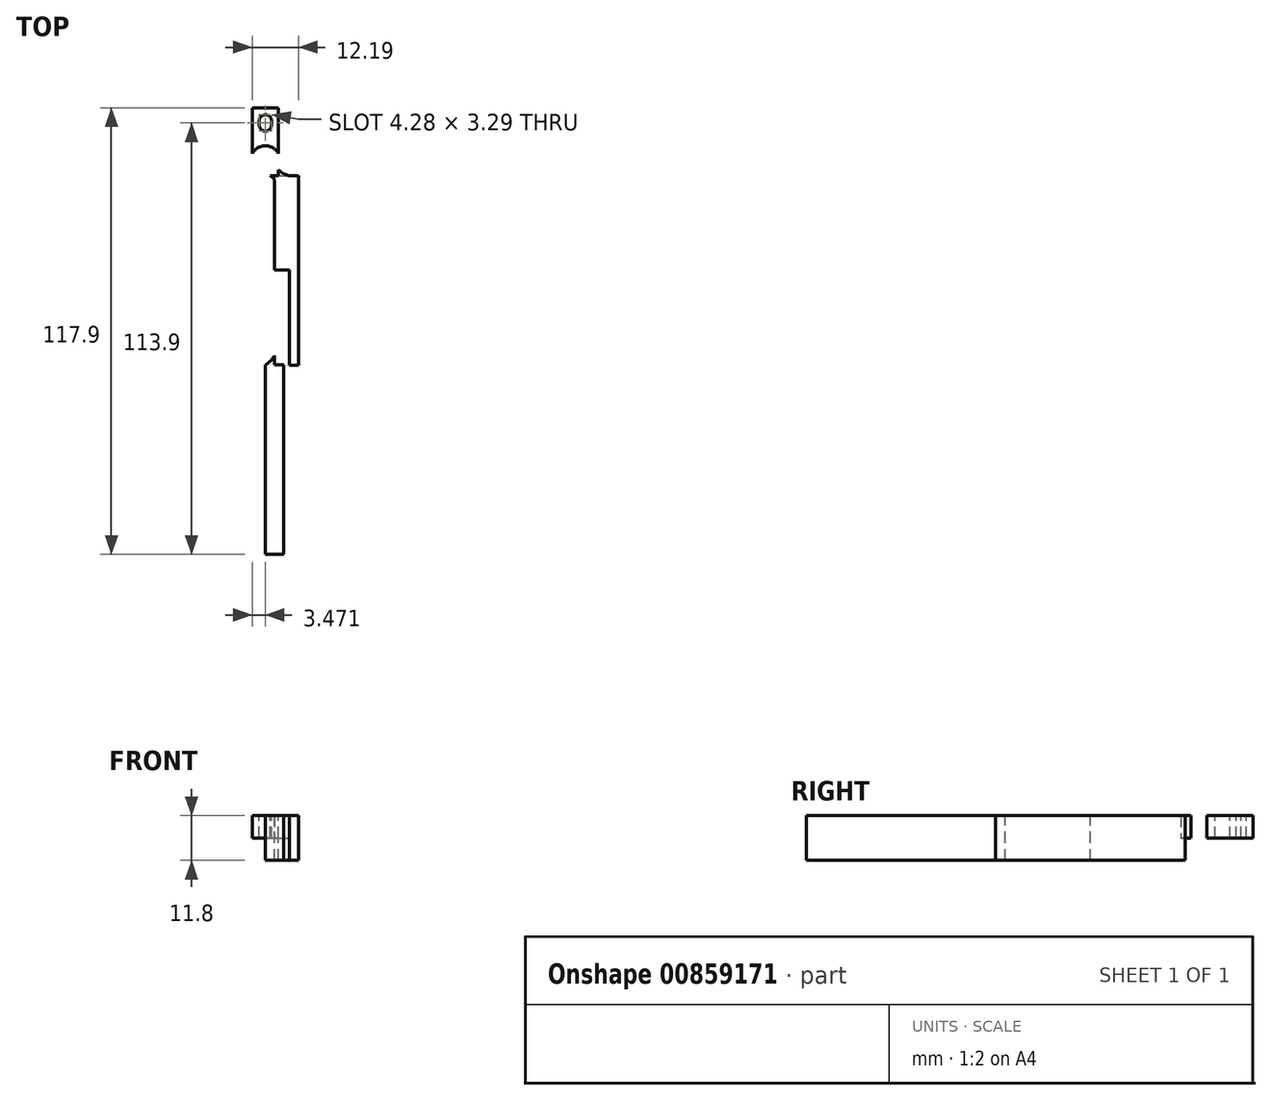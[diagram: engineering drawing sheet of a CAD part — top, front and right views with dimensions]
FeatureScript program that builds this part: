
annotation { "Feature Type Name" : "Feature", "Feature Type Description" : "" }
export const myFeature = defineFeature(function(context is Context, id is Id, definition is map)
    precondition{}
    {
        {
            var Q0;
            Q0=qCreatedBy(makeId("Top.planeOp"),FACE);
            var sketch = newSketch(context, id + "F0", { "sketchPlane" : qUnion([Q0])});
            skLineSegment(sketch, "E0.bottom", {"start": v(0, 0) * mm, "end": v(6.95, 0) * mm});
            skLineSegment(sketch, "E0.top", {"start": v(0, 17.9) * mm, "end": v(6.95, 17.9) * mm});
            skLineSegment(sketch, "E0.left", {"start": v(0, 0) * mm, "end": v(0, 17.9) * mm});
            skLineSegment(sketch, "E0.right", {"start": v(6.95, 0) * mm, "end": v(6.95, 17.9) * mm});
            skLineSegment(sketch, "E1", {"start": v(0, 0) * mm, "end": v(0, 7.85) * mm});
            skLineSegment(sketch, "E2", {"start": v(3.48, 0) * mm, "end": v(3.48, 7.85) * mm});
            skLineSegment(sketch, "E3", {"start": v(3.48, 7.85) * mm, "end": v(3.48, 6.9) * mm});
            skCircle(sketch, "E4", {"center": v(3.48, 3.92) * mm, "radius": 3.92 * mm});
            skLineSegment(sketch, "E5", {"start": v(3.47, 17.9) * mm, "end": v(3.47, 16.05) * mm});
            skLineSegment(sketch, "E6", {"start": v(3.47, 16.05) * mm, "end": v(3.48, 11.75) * mm});
            skLineSegment(sketch, "E7", {"start": v(3.47, 13.9) * mm, "end": v(3.47, 16.05) * mm});
            skLineSegment(sketch, "E8", {"start": v(3.48, 11.75) * mm, "end": v(3.47, 13.9) * mm});
            skLineSegment(sketch, "E9", {"start": v(4.55, 12.83) * mm, "end": v(4.55, 14.98) * mm});
            skLineSegment(sketch, "E10.bottom", {"start": v(3.48, 0) * mm, "end": v(1.03, 0) * mm});
            skLineSegment(sketch, "E10.top", {"start": v(3.48, -100) * mm, "end": v(1.03, -100) * mm});
            skLineSegment(sketch, "E10.left", {"start": v(3.48, 0) * mm, "end": v(3.48, -100) * mm});
            skLineSegment(sketch, "E10.right", {"start": v(1.03, 0) * mm, "end": v(1.03, -100) * mm});
            skLineSegment(sketch, "E11.bottom", {"start": v(3.48, 0) * mm, "end": v(5.93, 0) * mm});
            skLineSegment(sketch, "E11.top", {"start": v(3.48, -100) * mm, "end": v(5.93, -100) * mm});
            skLineSegment(sketch, "E11.right", {"start": v(5.93, 0) * mm, "end": v(5.93, -100) * mm});
            skLineSegment(sketch, "E12", {"start": v(5.93, 0) * mm, "end": v(5.93, 1.16) * mm});
            skLineSegment(sketch, "E13", {"start": v(1.03, 0) * mm, "end": v(1.02, 1.22) * mm});
            skLineSegment(sketch, "E14.bottom", {"start": v(6.95, 0) * mm, "end": v(9.83, -0.08) * mm});
            skLineSegment(sketch, "E14.left", {"start": v(6.95, 0) * mm, "end": v(6.95, 1.5) * mm});
            skLineSegment(sketch, "E15.right", {"start": v(5.93, -0.08) * mm, "end": v(5.93, -100) * mm});
            skLineSegment(sketch, "E16", {"start": v(3.48, 0) * mm, "end": v(3.48, -12.11) * mm});
            skLineSegment(sketch, "E17", {"start": v(3.48, 0) * mm, "end": v(3.48, -25) * mm});
            skLineSegment(sketch, "E18", {"start": v(3.48, -25) * mm, "end": v(1.03, -25) * mm});
            skLineSegment(sketch, "E19", {"start": v(1.03, -25) * mm, "end": v(1.03, -25.71) * mm});
            skLineSegment(sketch, "E20", {"start": v(1.03, -25) * mm, "end": v(1.03, -30) * mm});
            skLineSegment(sketch, "E21", {"start": v(5.93, -25) * mm, "end": v(5.93, -50) * mm});
            skPoint(sketch, "E21.startSnap0", {"position": v(2.25, -25) * mm});
            skLineSegment(sketch, "E22", {"start": v(5.93, -50) * mm, "end": v(9.83, -50.04) * mm});
            skLineSegment(sketch, "E23", {"start": v(3.48, -50) * mm, "end": v(1.03, -50) * mm});
            skLineSegment(sketch, "E24", {"start": v(5.93, -25) * mm, "end": v(9.83, -25) * mm});
            skLineSegment(sketch, "E25", {"start": v(5.93, -25) * mm, "end": v(5.93, -21.38) * mm});
            skLineSegment(sketch, "E26", {"start": v(5.93, -25) * mm, "end": v(5.93, -22.99) * mm});
            skLineSegment(sketch, "E27", {"start": v(3.48, -25) * mm, "end": v(3.48, -26.23) * mm});
            skLineSegment(sketch, "E28", {"start": v(5.93, -50) * mm, "end": v(5.93, -52.01) * mm});
            skLineSegment(sketch, "E29", {"start": v(3.48, -50) * mm, "end": v(3.48, -48.78) * mm});
            skLineSegment(sketch, "E30", {"start": v(5.93, -25) * mm, "end": v(5.93, -26.95) * mm});
            skLineSegment(sketch, "E31", {"start": v(3.48, -50) * mm, "end": v(5.93, -50) * mm});
            skLineSegment(sketch, "E32", {"start": v(3.48, 0) * mm, "end": v(3.48, -1.23) * mm});
            skLineSegment(sketch, "E33", {"start": v(6.95, 0) * mm, "end": v(6.95, 1.44) * mm});
            skFitSpline(sketch, "E34", {"points": [v(6.95, 1.5) * mm, v(9.83, -0.08) * mm], "startDerivative": vector(2.42, -2.4) * mm, "endDerivative": vector(3.34, -1.08) * mm});
            skLineSegment(sketch, "E35", {"start": v(1.03, 0) * mm, "end": v(1.03, -0.69) * mm});
            skLineSegment(sketch, "E36", {"start": v(1.03, 0) * mm, "end": v(1.03, -1) * mm});
            skLineSegment(sketch, "E37", {"start": v(5.92, 0) * mm, "end": v(5.93, -1.23) * mm});
            skFitSpline(sketch, "E38", {"points": [v(4.7, 0) * mm, v(5.93, -1.23) * mm], "startDerivative": vector(1.66, -0.95) * mm, "endDerivative": vector(0.86, -1.52) * mm});
            skLineSegment(sketch, "E39", {"start": v(5.93, -25) * mm, "end": v(5.93, -28.9) * mm});
            skLineSegment(sketch, "E40", {"start": v(3.48, -25) * mm, "end": v(5.93, -25) * mm});
            skLineSegment(sketch, "E41", {"start": v(5.93, -25) * mm, "end": v(5.93, -22.55) * mm});
            skLineSegment(sketch, "E42", {"start": v(5.93, -50) * mm, "end": v(5.93, -47.55) * mm});
            skFitSpline(sketch, "E43", {"points": [v(5.93, -47.55) * mm, v(3.48, -50) * mm], "startDerivative": vector(-2.07, -3.53) * mm, "endDerivative": vector(-2.94, -2.05) * mm});
            skLineSegment(sketch, "E44.left", {"start": v(5.93, -50) * mm, "end": v(5.93, -100) * mm});
            skLineSegment(sketch, "E45", {"start": v(9.83, -0.08) * mm, "end": v(9.83, -50.04) * mm});
            skLineSegment(sketch, "E46.bottom", {"start": v(9.83, -0.08) * mm, "end": v(12.2, -0.08) * mm});
            skLineSegment(sketch, "E46.top", {"start": v(9.83, -50.08) * mm, "end": v(12.2, -50.08) * mm});
            skLineSegment(sketch, "E46.left", {"start": v(9.83, -0.08) * mm, "end": v(9.83, -50.08) * mm});
            skLineSegment(sketch, "E46.right", {"start": v(12.2, -0.08) * mm, "end": v(12.2, -50.08) * mm});
            skLineSegment(sketch, "E47.bottom", {"start": v(5.93, -50) * mm, "end": v(8.3, -50) * mm});
            skLineSegment(sketch, "E47.top", {"start": v(5.93, -100) * mm, "end": v(8.3, -100) * mm});
            skLineSegment(sketch, "E47.right", {"start": v(8.3, -50) * mm, "end": v(8.3, -100) * mm});
            skLineSegment(sketch, "E48", {"start": v(8.3, -50) * mm, "end": v(12.2, -50.08) * mm});
            skLineSegment(sketch, "E49", {"start": v(8.3, -50) * mm, "end": v(8.3, -53.9) * mm});
            skFitSpline(sketch, "E50", {"points": [v(8.3, -53.9) * mm, v(10.24, -50.04) * mm], "startDerivative": vector(0.85, 4.55) * mm, "endDerivative": vector(3.1, 3.55) * mm});
            skCircle(sketch, "E51", {"center": v(3.48, 3.92) * mm, "radius": 3.28 * mm});
            skLineSegment(sketch, "E52", {"start": v(3.47, 13.9) * mm, "end": v(3.47, 12.9) * mm});
            skLineSegment(sketch, "E53", {"start": v(3.47, 13.9) * mm, "end": v(3.47, 14.9) * mm});
            skCircle(sketch, "E54", {"center": v(3.47, 13.4) * mm, "radius": 1.64 * mm});
            skArc(sketch, "E55", {"start": v(5.1, 14.7) * mm, "mid": v(1.83, 14.37) * mm, "end": v(5.1, 14.14) * mm});
            skLineSegment(sketch, "E56", {"start": v(3.48, 11.75) * mm, "end": v(1.27, 11.75) * mm});
            skLineSegment(sketch, "E57", {"start": v(3.48, 11.75) * mm, "end": v(5.93, 11.75) * mm});
            skLineSegment(sketch, "E58", {"start": v(3.47, 16.05) * mm, "end": v(1.21, 16.05) * mm});
            skLineSegment(sketch, "E59", {"start": v(3.47, 16.05) * mm, "end": v(5.69, 16.05) * mm});
            skLineSegment(sketch, "E60", {"start": v(5.11, 13.43) * mm, "end": v(5.1, 14.7) * mm});
            skLineSegment(sketch, "E61", {"start": v(1.84, 13.46) * mm, "end": v(1.83, 14.38) * mm});
            skSolve(sketch);
        }
        {
            var Q0;
            {var subQ0=sQuery(id+"F0.wireOp",EDGE,"E4");var subQ3=sQuery(id+"F0.wireOp",EDGE,"E0.right");var subQ10=makeQuery(id+"F0.imprint","INTERSECT",VERTEX,{"disambiguationData":[OD(0.0)],"derivedFrom":[subQ3,subQ0]});Q0=makeQuery(id+"F0.imprint","IMPRINT",FACE,{"disambiguationData":[TD([[makeQuery(id+"F0.imprint","IMPRINT",EDGE,{"disambiguationData":[TD([[subQ10,-1.0]])],"derivedFrom":subQ3}),1.0]])]});}
            var Q1;
            {var subQ0=sQuery(id+"F0.wireOp",EDGE,"E4");var subQ7=sQuery(id+"F0.wireOp",EDGE,"E1");var subQ10=makeQuery(id+"F0.imprint","INTERSECT",VERTEX,{"disambiguationData":[OD(0.0)],"derivedFrom":[subQ7,subQ0]});Q1=makeQuery(id+"F0.imprint","IMPRINT",FACE,{"disambiguationData":[TD([[makeQuery(id+"F0.imprint","IMPRINT",EDGE,{"disambiguationData":[TD([[subQ10,-1.0]])],"derivedFrom":subQ7}),-1.0]])]});}
            var Q2;
            {var subQ0=sQuery(id+"F0.wireOp",EDGE,"E1");var subQ1=sQuery(id+"F0.wireOp",EDGE,"E0.bottom");var subQ2=makeQuery(id+"F0.imprint","INTERSECT",VERTEX,{"derivedFrom":[subQ1,subQ0]});Q2=makeQuery(id+"F0.imprint","IMPRINT",FACE,{"disambiguationData":[TD([[makeQuery(id+"F0.imprint","IMPRINT",EDGE,{"disambiguationData":[TD([[subQ2,-1.0]])],"derivedFrom":subQ0}),-1.0]])]});}
            var Q3;
            {var subQ0=sQuery(id+"F0.wireOp",EDGE,"E10.bottom");Q3=makeQuery(id+"F0.imprint","IMPRINT",FACE,{"disambiguationData":[TD([[makeQuery(id+"F0.imprint","IMPRINT",EDGE,{"derivedFrom":subQ0}),-1.0]])]});}
            var Q4;
            {var subQ0=sQuery(id+"F0.wireOp",EDGE,"E4");var subQ1=sQuery(id+"F0.wireOp",EDGE,"E1");var subQ2=makeQuery(id+"F0.imprint","INTERSECT",VERTEX,{"disambiguationData":[OD(0.0)],"derivedFrom":[subQ1,subQ0]});Q4=makeQuery(id+"F0.imprint","IMPRINT",FACE,{"disambiguationData":[TD([[makeQuery(id+"F0.imprint","IMPRINT",EDGE,{"disambiguationData":[TD([[subQ2,-1.0]])],"derivedFrom":subQ1}),1.0]])]});}
            var Q5;
            {var subQ0=sQuery(id+"F0.wireOp",EDGE,"E4");var subQ1=sQuery(id+"F0.wireOp",EDGE,"E0.right");var subQ2=makeQuery(id+"F0.imprint","INTERSECT",VERTEX,{"disambiguationData":[OD(0.0)],"derivedFrom":[subQ1,subQ0]});Q5=makeQuery(id+"F0.imprint","IMPRINT",FACE,{"disambiguationData":[TD([[makeQuery(id+"F0.imprint","IMPRINT",EDGE,{"disambiguationData":[TD([[subQ2,-1.0]])],"derivedFrom":subQ1}),-1.0]])]});}
            var Q6;
            {var subQ5=sQuery(id+"F0.wireOp",EDGE,"E14.left");Q6=makeQuery(id+"F0.imprint","IMPRINT",FACE,{"disambiguationData":[TD([[makeQuery(id+"F0.imprint","IMPRINT",EDGE,{"derivedFrom":subQ5}),1.0]])]});}
            var Q7;
            {var subQ0=sQuery(id+"F0.wireOp",EDGE,"E11.bottom");var subQ5=makeQuery(id+"F0.imprint","INTERSECT",VERTEX,{"derivedFrom":[subQ0,sQuery(id+"F0.wireOp",EDGE,"E38")]});Q7=makeQuery(id+"F0.imprint","IMPRINT",FACE,{"disambiguationData":[TD([[makeQuery(id+"F0.imprint","IMPRINT",EDGE,{"disambiguationData":[TD([[subQ5,-1.0]])],"derivedFrom":subQ0}),1.0]])]});}
            var Q8;
            {var subQ3=sQuery(id+"F0.wireOp",EDGE,"E38");Q8=makeQuery(id+"F0.imprint","IMPRINT",FACE,{"disambiguationData":[TD([[makeQuery(id+"F0.imprint","IMPRINT",EDGE,{"derivedFrom":subQ3}),1.0]])]});}
            var Q9;
            Q9=makeQuery(id+"F0.imprint","IMPRINT",FACE,{"disambiguationData":[TD([[makeQuery(id+"F0.imprint","IMPRINT",EDGE,{"derivedFrom":sQuery(id+"F0.wireOp",EDGE,"E14.bottom")}),1.0]])]});
            extrude(context, id + "F1", {"entities" : qUnion([Q0, Q1, Q2, Q3, Q4, Q5, Q6, Q7, Q8, Q9]), "depth" : -5.9 * mm, "offsetDistance" : 25 * mm});
        }
        {
            var Q0;
            {var subQ1=sQuery(id+"F0.wireOp",EDGE,"E47.top");Q0=makeQuery(id+"F0.imprint","IMPRINT",FACE,{"disambiguationData":[TD([[makeQuery(id+"F0.imprint","IMPRINT",EDGE,{"derivedFrom":subQ1}),1.0]])]});}
            var Q1;
            Q1=makeQuery(id+"F0.imprint","IMPRINT",FACE,{"disambiguationData":[TD([[makeQuery(id+"F0.imprint","IMPRINT",EDGE,{"derivedFrom":sQuery(id+"F0.wireOp",EDGE,"E31")}),1.0]])]});
            var Q2;
            {var subQ2=sQuery(id+"F0.wireOp",EDGE,"E11.top");Q2=makeQuery(id+"F0.imprint","IMPRINT",FACE,{"disambiguationData":[TD([[makeQuery(id+"F0.imprint","IMPRINT",EDGE,{"derivedFrom":subQ2}),1.0]])]});}
            var Q3;
            {var subQ3=sQuery(id+"F0.wireOp",EDGE,"E22");var subQ5=sQuery(id+"F0.wireOp",EDGE,"E46.left");var subQ6=makeQuery(id+"F0.imprint","INTERSECT",VERTEX,{"derivedFrom":[subQ3,subQ5]});Q3=makeQuery(id+"F0.imprint","IMPRINT",FACE,{"disambiguationData":[TD([[makeQuery(id+"F0.imprint","IMPRINT",EDGE,{"disambiguationData":[TD([[subQ6,1.0]])],"derivedFrom":subQ3}),-1.0]])]});}
            var Q4;
            {var subQ7=sQuery(id+"F0.wireOp",EDGE,"E21");Q4=makeQuery(id+"F0.imprint","IMPRINT",FACE,{"disambiguationData":[TD([[makeQuery(id+"F0.imprint","IMPRINT",EDGE,{"derivedFrom":subQ7}),1.0]])]});}
            var Q5;
            {var subQ6=sQuery(id+"F0.wireOp",EDGE,"E46.bottom");Q5=makeQuery(id+"F0.imprint","IMPRINT",FACE,{"disambiguationData":[TD([[makeQuery(id+"F0.imprint","IMPRINT",EDGE,{"derivedFrom":subQ6}),-1.0]])]});}
            var Q6;
            {var subQ3=sQuery(id+"F0.wireOp",EDGE,"E46.left");var subQ6=sQuery(id+"F0.wireOp",EDGE,"E46.top");var subQ7=makeQuery(id+"F0.imprint","INTERSECT",VERTEX,{"derivedFrom":[subQ6,subQ3]});Q6=makeQuery(id+"F0.imprint","IMPRINT",FACE,{"disambiguationData":[TD([[makeQuery(id+"F0.imprint","IMPRINT",EDGE,{"disambiguationData":[TD([[subQ7,-1.0]])],"derivedFrom":subQ6}),1.0]])]});}
            var Q7;
            {var subQ0=sQuery(id+"F0.wireOp",EDGE,"E48");var subQ3=sQuery(id+"F0.wireOp",EDGE,"E50");var subQ5=makeQuery(id+"F0.imprint","INTERSECT",VERTEX,{"derivedFrom":[subQ0,subQ3]});Q7=makeQuery(id+"F0.imprint","IMPRINT",FACE,{"disambiguationData":[TD([[makeQuery(id+"F0.imprint","IMPRINT",EDGE,{"disambiguationData":[TD([[subQ5,1.0]])],"derivedFrom":subQ3}),-1.0]])]});}
            var Q8;
            {var subQ0=sQuery(id+"F0.wireOp",EDGE,"E46.left");var subQ1=sQuery(id+"F0.wireOp",EDGE,"E22");var subQ2=makeQuery(id+"F0.imprint","INTERSECT",VERTEX,{"derivedFrom":[subQ1,subQ0]});Q8=makeQuery(id+"F0.imprint","IMPRINT",FACE,{"disambiguationData":[TD([[makeQuery(id+"F0.imprint","IMPRINT",EDGE,{"disambiguationData":[TD([[subQ2,1.0]])],"derivedFrom":subQ1}),1.0]])]});}
            var Q9;
            {var subQ0=sQuery(id+"F0.wireOp",EDGE,"E47.bottom");Q9=makeQuery(id+"F0.imprint","IMPRINT",FACE,{"disambiguationData":[TD([[makeQuery(id+"F0.imprint","IMPRINT",EDGE,{"derivedFrom":subQ0}),-1.0]])]});}
            var Q10;
            {var subQ4=sQuery(id+"F0.wireOp",EDGE,"E14.bottom");Q10=makeQuery(id+"F0.imprint","IMPRINT",FACE,{"disambiguationData":[TD([[makeQuery(id+"F0.imprint","IMPRINT",EDGE,{"derivedFrom":subQ4}),-1.0]])]});}
            extrude(context, id + "F2", {"entities" : qUnion([Q0, Q1, Q2, Q3, Q4, Q5, Q6, Q7, Q8, Q9, Q10]), "operationType" : NewBodyOperationType.ADD, "depth" : -11.8 * mm, "offsetDistance" : 25 * mm});
        }
        {
            var Q0;
            {var subQ15=sQuery(id+"F0.wireOp",EDGE,"E0.left");Q0=makeQuery(id+"F0.imprint","IMPRINT",FACE,{"disambiguationData":[TD([[makeQuery(id+"F0.imprint","IMPRINT",EDGE,{"derivedFrom":subQ15}),-1.0]])]});}
            extrude(context, id + "F3", {"entities" : qUnion([Q0]), "operationType" : NewBodyOperationType.ADD, "depth" : -2.5 * mm, "offsetDistance" : 25 * mm});
        }
    });
